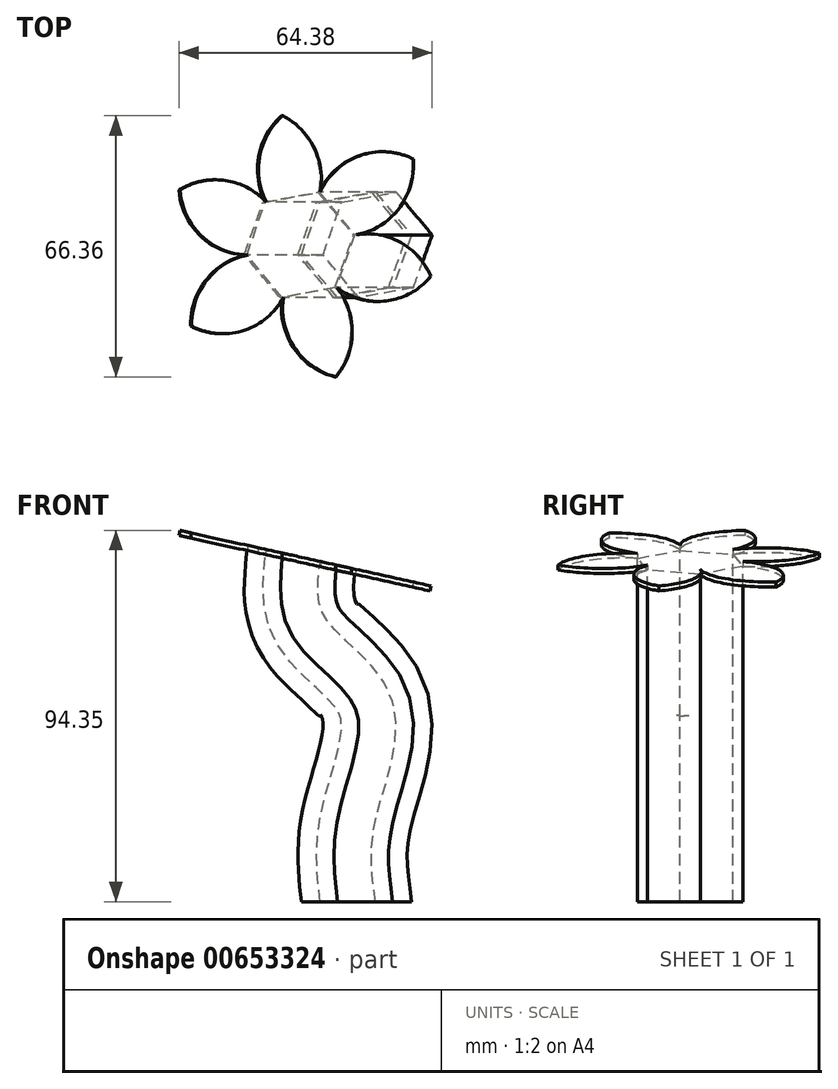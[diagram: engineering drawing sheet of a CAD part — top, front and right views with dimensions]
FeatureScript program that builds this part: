
annotation { "Feature Type Name" : "Feature", "Feature Type Description" : "" }
export const myFeature = defineFeature(function(context is Context, id is Id, definition is map)
    precondition{}
    {
        {
            var Q0;
            Q0=qCreatedBy(makeId("Top.planeOp"),FACE);
            var sketch = newSketch(context, id + "F0", { "sketchPlane" : qUnion([Q0])});
            skPoint(sketch, "E0.0.midPoint", {"position": v(1.83, 13.08) * mm});
            skCircle(sketch, "E1.cCircle", {"center": v(0, 0) * mm, "radius": 12.33 * mm, "construction": true});
            skLineSegment(sketch, "E1.0", {"start": v(4.8, 13.4) * mm, "end": v(14, 2.55) * mm});
            skLineSegment(sketch, "E1.1", {"start": v(14, 2.55) * mm, "end": v(9.2, -10.86) * mm});
            skLineSegment(sketch, "E1.2", {"start": v(9.2, -10.86) * mm, "end": v(-4.8, -13.4) * mm});
            skLineSegment(sketch, "E1.3", {"start": v(-4.8, -13.4) * mm, "end": v(-14, -2.55) * mm});
            skLineSegment(sketch, "E1.4", {"start": v(-14, -2.55) * mm, "end": v(-9.2, 10.86) * mm});
            skLineSegment(sketch, "E1.5", {"start": v(-9.2, 10.86) * mm, "end": v(4.8, 13.4) * mm});
            skPoint(sketch, "E1.0.midPoint", {"position": v(9.4, 7.98) * mm});
            skSolve(sketch);
        }
        {
            var Q0;
            Q0=qCreatedBy(makeId("Front.planeOp"),FACE);
            var sketch = newSketch(context, id + "F1", { "sketchPlane" : qUnion([Q0])});
            skFitSpline(sketch, "E2", {"points": [v(0, 0) * mm, v(0, 20.78) * mm, v(4.5, 50) * mm, v(-11.97, 69.54) * mm, v(-14.17, 86.24) * mm], "startDerivative": vector(-10.26, 81.4) * mm, "endDerivative": vector(7.5, 80.94) * mm});
            skSolve(sketch);
        }
        {
            var Q0;
            Q0=makeQuery(id+"F0.imprint","IMPRINT",FACE,{"disambiguationData":[TD([[makeQuery(id+"F0.imprint","IMPRINT",EDGE,{"derivedFrom":sQuery(id+"F0.wireOp",EDGE,"E1.0")}),-1.0]])]});
            var Q1;
            Q1=sQuery(id+"F1.wireOp",EDGE,"E2");
            sweep(context, id + "F2", {"profiles" : qUnion([Q0]), "path" : qUnion([Q1])});
        }
        {
            var Q0;
            Q0=makeQuery(id+"F2.opSweep","CAP_FACE",FACE,{"disambiguationData":[OSD([sQuery(id+"F0.wireOp",EDGE,"E1.0"),sQuery(id+"F0.wireOp",EDGE,"E1.1"),sQuery(id+"F0.wireOp",EDGE,"E1.2"),sQuery(id+"F0.wireOp",EDGE,"E1.3"),sQuery(id+"F0.wireOp",EDGE,"E1.4"),sQuery(id+"F0.wireOp",EDGE,"E1.5"),sQuery(id+"F1.wireOp",VERTEX,"E2.end")])],"isStart":false});
            var sketch = newSketch(context, id + "F3", { "sketchPlane" : qUnion([Q0])});
            skArc(sketch, "E3", {"start": v(-3.43, 21.8) * mm, "mid": v(-17.3, 22.68) * mm, "end": v(-27.66, 13.4) * mm});
            skArc(sketch, "E4", {"start": v(-18.45, 2.55) * mm, "mid": v(-7.18, 9.24) * mm, "end": v(-3.43, 21.8) * mm});
            skArc(sketch, "E5", {"start": v(-23.25, -10.86) * mm, "mid": v(-10.47, -14.23) * mm, "end": v(1.16, -7.97) * mm});
            skArc(sketch, "E6", {"start": v(1.16, -7.97) * mm, "mid": v(-6.82, 0.68) * mm, "end": v(-18.45, 2.55) * mm});
            skArc(sketch, "E7", {"start": v(-23.49, -33.54) * mm, "mid": v(-19.34, -22.24) * mm, "end": v(-23.25, -10.86) * mm});
            skArc(sketch, "E8", {"start": v(-37.25, -13.4) * mm, "mid": v(-34.3, -26.16) * mm, "end": v(-23.49, -33.54) * mm});
            skArc(sketch, "E9", {"start": v(-61.09, -20.62) * mm, "mid": v(-47.72, -21.8) * mm, "end": v(-37.25, -13.4) * mm});
            skArc(sketch, "E10", {"start": v(-46.46, -2.55) * mm, "mid": v(-57.09, -8.9) * mm, "end": v(-61.09, -20.62) * mm});
            skArc(sketch, "E11", {"start": v(-64.15, 13.92) * mm, "mid": v(-58.48, 2.28) * mm, "end": v(-46.46, -2.55) * mm});
            skArc(sketch, "E12", {"start": v(-41.67, 10.86) * mm, "mid": v(-52.37, 16.38) * mm, "end": v(-64.15, 13.92) * mm});
            skArc(sketch, "E13", {"start": v(-37.41, 32.82) * mm, "mid": v(-43.37, 22.58) * mm, "end": v(-41.67, 10.86) * mm});
            skArc(sketch, "E14", {"start": v(-27.66, 13.4) * mm, "mid": v(-29.28, 24.75) * mm, "end": v(-37.41, 32.82) * mm});
            skSolve(sketch);
        }
        {
            var Q0;
            Q0 = qSketchRegion(id + "F3", true);
            extrude(context, id + "F4", {"entities" : qUnion([Q0]), "operationType" : NewBodyOperationType.ADD, "depth" : 1.3 * mm, "offsetDistance" : 25 * mm});
        }
    });
